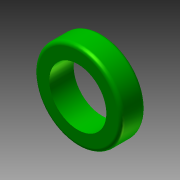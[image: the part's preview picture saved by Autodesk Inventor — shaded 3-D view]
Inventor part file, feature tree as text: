
AUTODESK INVENTOR PART (.ipt)
format: ipt  version: 2012 (Build 160160000, 160)  size: 107,520 bytes
history: native  units: in
note: dims shown in document units (in); Inventor stores cm internally (conversion verified against a paired STEP export)
features: extrude x1, fillet x1, sketch x1
ambient origin geometry x8: Origin, YZ Plane, XZ Plane, XY Plane, X Axis, Y Axis, Z Axis, Center Point
bodies: Solid1 (feature_tree)
feature tree (3):
  extrude  "Extrusion1"  Depth=2.875in
  fillet  "Fillet1"  Radius=0.8in
  sketch  "Sketch1"  dims[d0=1.875in d1=2.875in d2=0.8in d3=0.0in d4=0.125in]
